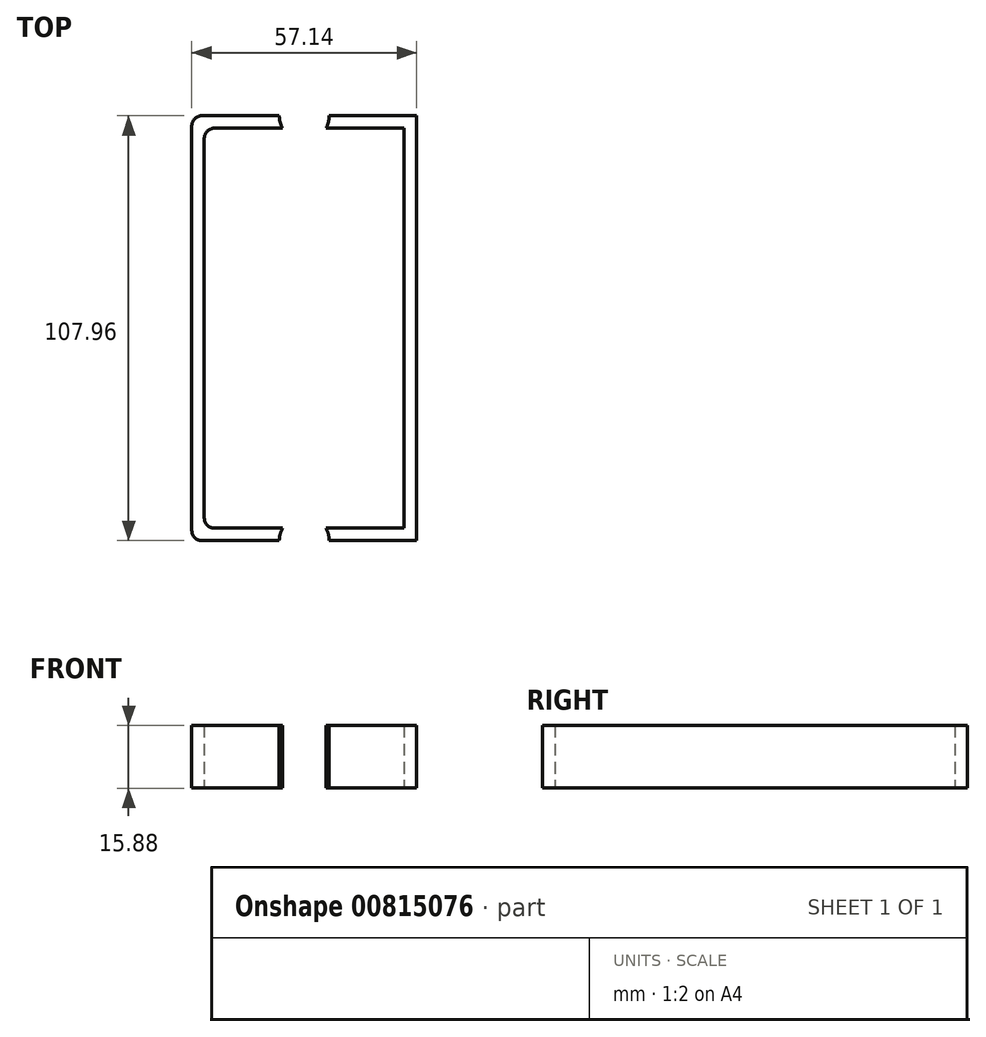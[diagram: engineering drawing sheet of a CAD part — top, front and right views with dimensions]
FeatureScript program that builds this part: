
annotation { "Feature Type Name" : "Feature", "Feature Type Description" : "" }
export const myFeature = defineFeature(function(context is Context, id is Id, definition is map)
    precondition{}
    {
        {
            var Q0;
            Q0=qCreatedBy(makeId("Top.planeOp"),FACE);
            var sketch = newSketch(context, id + "F0", { "sketchPlane" : qUnion([Q0])});
            skLineSegment(sketch, "E0.bottom", {"start": v(-25.4, 50.8) * mm, "end": v(25.4, 50.8) * mm});
            skLineSegment(sketch, "E0.top", {"start": v(-25.4, -50.8) * mm, "end": v(25.4, -50.8) * mm});
            skLineSegment(sketch, "E0.left", {"start": v(-25.4, 50.8) * mm, "end": v(-25.4, -50.8) * mm});
            skLineSegment(sketch, "E0.right", {"start": v(25.4, 50.8) * mm, "end": v(25.4, -50.8) * mm});
            skPoint(sketch, "E0.middle", {"position": v(0, 0) * mm});
            skLineSegment(sketch, "E1.bottom", {"start": v(-28.57, 53.98) * mm, "end": v(28.58, 53.98) * mm});
            skLineSegment(sketch, "E1.top", {"start": v(-28.58, -53.98) * mm, "end": v(28.57, -53.98) * mm});
            skLineSegment(sketch, "E1.left", {"start": v(-28.57, 53.98) * mm, "end": v(-28.58, -53.98) * mm});
            skLineSegment(sketch, "E1.right", {"start": v(28.58, 53.98) * mm, "end": v(28.57, -53.98) * mm});
            skCircle(sketch, "E2", {"center": v(0, 53.98) * mm, "radius": 6.35 * mm});
            skCircle(sketch, "E3", {"center": v(-28.57, 53.98) * mm, "radius": 6.35 * mm});
            skCircle(sketch, "E4", {"center": v(-28.58, -53.98) * mm, "radius": 6.35 * mm});
            skCircle(sketch, "E5", {"center": v(0, -53.98) * mm, "radius": 6.35 * mm});
            skSolve(sketch);
        }
        {
            var Q0;
            {var subQ0=sQuery(id+"F0.wireOp",EDGE,"E1.left");var subQ1=sQuery(id+"F0.wireOp",EDGE,"E1.bottom");var subQ2=makeQuery(id+"F0.imprint","INTERSECT",VERTEX,{"derivedFrom":[subQ1,subQ0]});Q0=makeQuery(id+"F0.imprint","IMPRINT",FACE,{"disambiguationData":[TD([[makeQuery(id+"F0.imprint","IMPRINT",EDGE,{"disambiguationData":[TD([[subQ2,-1.0]])],"derivedFrom":subQ1}),1.0]])]});}
            var Q1;
            {var subQ0=sQuery(id+"F0.wireOp",EDGE,"E2");var subQ1=sQuery(id+"F0.wireOp",EDGE,"E1.bottom");var subQ2=makeQuery(id+"F0.imprint","INTERSECT",VERTEX,{"disambiguationData":[OD(0.0)],"derivedFrom":[subQ1,subQ0]});Q1=makeQuery(id+"F0.imprint","IMPRINT",FACE,{"disambiguationData":[TD([[makeQuery(id+"F0.imprint","IMPRINT",EDGE,{"disambiguationData":[TD([[subQ2,-1.0]])],"derivedFrom":subQ1}),1.0]])]});}
            var Q2;
            {var subQ0=sQuery(id+"F0.wireOp",EDGE,"E1.left");var subQ1=sQuery(id+"F0.wireOp",EDGE,"E1.top");var subQ2=makeQuery(id+"F0.imprint","INTERSECT",VERTEX,{"derivedFrom":[subQ1,subQ0]});Q2=makeQuery(id+"F0.imprint","IMPRINT",FACE,{"disambiguationData":[TD([[makeQuery(id+"F0.imprint","IMPRINT",EDGE,{"disambiguationData":[TD([[subQ2,-1.0]])],"derivedFrom":subQ1}),-1.0]])]});}
            var Q3;
            {var subQ0=sQuery(id+"F0.wireOp",EDGE,"E5");var subQ1=sQuery(id+"F0.wireOp",EDGE,"E1.top");var subQ2=makeQuery(id+"F0.imprint","INTERSECT",VERTEX,{"disambiguationData":[OD(0.0)],"derivedFrom":[subQ1,subQ0]});Q3=makeQuery(id+"F0.imprint","IMPRINT",FACE,{"disambiguationData":[TD([[makeQuery(id+"F0.imprint","IMPRINT",EDGE,{"disambiguationData":[TD([[subQ2,-1.0]])],"derivedFrom":subQ1}),-1.0]])]});}
            var Q4;
            {var subQ0=sQuery(id+"F0.wireOp",EDGE,"E3");var subQ1=sQuery(id+"F0.wireOp",EDGE,"E0.bottom");var subQ2=makeQuery(id+"F0.imprint","INTERSECT",VERTEX,{"derivedFrom":[subQ1,subQ0]});Q4=makeQuery(id+"F0.imprint","IMPRINT",FACE,{"disambiguationData":[TD([[makeQuery(id+"F0.imprint","IMPRINT",EDGE,{"disambiguationData":[TD([[subQ2,-1.0]])],"derivedFrom":subQ1}),1.0]])]});}
            var Q5;
            {var subQ0=sQuery(id+"F0.wireOp",EDGE,"E4");var subQ1=sQuery(id+"F0.wireOp",EDGE,"E0.top");var subQ2=makeQuery(id+"F0.imprint","INTERSECT",VERTEX,{"derivedFrom":[subQ1,subQ0]});Q5=makeQuery(id+"F0.imprint","IMPRINT",FACE,{"disambiguationData":[TD([[makeQuery(id+"F0.imprint","IMPRINT",EDGE,{"disambiguationData":[TD([[subQ2,-1.0]])],"derivedFrom":subQ1}),-1.0]])]});}
            var Q6;
            {var subQ0=sQuery(id+"F0.wireOp",EDGE,"E3");var subQ1=sQuery(id+"F0.wireOp",EDGE,"E0.left");var subQ2=makeQuery(id+"F0.imprint","INTERSECT",VERTEX,{"derivedFrom":[subQ1,subQ0]});Q6=makeQuery(id+"F0.imprint","IMPRINT",FACE,{"disambiguationData":[TD([[makeQuery(id+"F0.imprint","IMPRINT",EDGE,{"disambiguationData":[TD([[subQ2,-1.0]])],"derivedFrom":subQ1}),-1.0]])]});}
            var Q7;
            {var subQ5=sQuery(id+"F0.wireOp",EDGE,"E0.left");var subQ6=sQuery(id+"F0.wireOp",EDGE,"E0.bottom");var subQ7=makeQuery(id+"F0.imprint","INTERSECT",VERTEX,{"derivedFrom":[subQ6,subQ5]});Q7=makeQuery(id+"F0.imprint","IMPRINT",FACE,{"disambiguationData":[TD([[makeQuery(id+"F0.imprint","IMPRINT",EDGE,{"disambiguationData":[TD([[subQ7,-1.0]])],"derivedFrom":subQ6}),1.0]])]});}
            var Q8;
            {var subQ0=sQuery(id+"F0.wireOp",EDGE,"E2");var subQ1=sQuery(id+"F0.wireOp",EDGE,"E0.bottom");var subQ2=makeQuery(id+"F0.imprint","INTERSECT",VERTEX,{"disambiguationData":[OD(0.0)],"derivedFrom":[subQ1,subQ0]});Q8=makeQuery(id+"F0.imprint","IMPRINT",FACE,{"disambiguationData":[TD([[makeQuery(id+"F0.imprint","IMPRINT",EDGE,{"disambiguationData":[TD([[subQ2,-1.0]])],"derivedFrom":subQ1}),1.0]])]});}
            var Q9;
            {var subQ6=sQuery(id+"F0.wireOp",EDGE,"E0.left");var subQ7=sQuery(id+"F0.wireOp",EDGE,"E0.top");var subQ8=makeQuery(id+"F0.imprint","INTERSECT",VERTEX,{"derivedFrom":[subQ7,subQ6]});Q9=makeQuery(id+"F0.imprint","IMPRINT",FACE,{"disambiguationData":[TD([[makeQuery(id+"F0.imprint","IMPRINT",EDGE,{"disambiguationData":[TD([[subQ8,-1.0]])],"derivedFrom":subQ7}),-1.0]])]});}
            var Q10;
            {var subQ0=sQuery(id+"F0.wireOp",EDGE,"E5");var subQ1=sQuery(id+"F0.wireOp",EDGE,"E0.top");var subQ2=makeQuery(id+"F0.imprint","INTERSECT",VERTEX,{"disambiguationData":[OD(0.0)],"derivedFrom":[subQ1,subQ0]});Q10=makeQuery(id+"F0.imprint","IMPRINT",FACE,{"disambiguationData":[TD([[makeQuery(id+"F0.imprint","IMPRINT",EDGE,{"disambiguationData":[TD([[subQ2,-1.0]])],"derivedFrom":subQ1}),-1.0]])]});}
            extrude(context, id + "F1", {"entities" : qUnion([Q0, Q1, Q2, Q3, Q4, Q5, Q6, Q7, Q8, Q9, Q10]), "depth" : 3.17 * mm, "offsetDistance" : 25.4 * mm});
        }
        {
            var Q0;
            {var subQ0=sQuery(id+"F0.wireOp",EDGE,"E3");var subQ1=sQuery(id+"F0.wireOp",EDGE,"E0.bottom");var subQ2=makeQuery(id+"F0.imprint","INTERSECT",VERTEX,{"derivedFrom":[subQ1,subQ0]});Q0=makeQuery(id+"F0.imprint","IMPRINT",FACE,{"disambiguationData":[TD([[makeQuery(id+"F0.imprint","IMPRINT",EDGE,{"disambiguationData":[TD([[subQ2,-1.0]])],"derivedFrom":subQ1}),1.0]])]});}
            var Q1;
            {var subQ0=sQuery(id+"F0.wireOp",EDGE,"E2");var subQ1=sQuery(id+"F0.wireOp",EDGE,"E0.bottom");var subQ2=makeQuery(id+"F0.imprint","INTERSECT",VERTEX,{"disambiguationData":[OD(0.0)],"derivedFrom":[subQ1,subQ0]});Q1=makeQuery(id+"F0.imprint","IMPRINT",FACE,{"disambiguationData":[TD([[makeQuery(id+"F0.imprint","IMPRINT",EDGE,{"disambiguationData":[TD([[subQ2,-1.0]])],"derivedFrom":subQ1}),1.0]])]});}
            var Q2;
            {var subQ5=sQuery(id+"F0.wireOp",EDGE,"E0.left");var subQ6=sQuery(id+"F0.wireOp",EDGE,"E0.bottom");var subQ7=makeQuery(id+"F0.imprint","INTERSECT",VERTEX,{"derivedFrom":[subQ6,subQ5]});Q2=makeQuery(id+"F0.imprint","IMPRINT",FACE,{"disambiguationData":[TD([[makeQuery(id+"F0.imprint","IMPRINT",EDGE,{"disambiguationData":[TD([[subQ7,-1.0]])],"derivedFrom":subQ6}),1.0]])]});}
            var Q3;
            {var subQ0=sQuery(id+"F0.wireOp",EDGE,"E3");var subQ1=sQuery(id+"F0.wireOp",EDGE,"E0.left");var subQ2=makeQuery(id+"F0.imprint","INTERSECT",VERTEX,{"derivedFrom":[subQ1,subQ0]});Q3=makeQuery(id+"F0.imprint","IMPRINT",FACE,{"disambiguationData":[TD([[makeQuery(id+"F0.imprint","IMPRINT",EDGE,{"disambiguationData":[TD([[subQ2,-1.0]])],"derivedFrom":subQ1}),-1.0]])]});}
            var Q4;
            {var subQ6=sQuery(id+"F0.wireOp",EDGE,"E0.left");var subQ7=sQuery(id+"F0.wireOp",EDGE,"E0.top");var subQ8=makeQuery(id+"F0.imprint","INTERSECT",VERTEX,{"derivedFrom":[subQ7,subQ6]});Q4=makeQuery(id+"F0.imprint","IMPRINT",FACE,{"disambiguationData":[TD([[makeQuery(id+"F0.imprint","IMPRINT",EDGE,{"disambiguationData":[TD([[subQ8,-1.0]])],"derivedFrom":subQ7}),-1.0]])]});}
            var Q5;
            {var subQ0=sQuery(id+"F0.wireOp",EDGE,"E4");var subQ1=sQuery(id+"F0.wireOp",EDGE,"E0.top");var subQ2=makeQuery(id+"F0.imprint","INTERSECT",VERTEX,{"derivedFrom":[subQ1,subQ0]});Q5=makeQuery(id+"F0.imprint","IMPRINT",FACE,{"disambiguationData":[TD([[makeQuery(id+"F0.imprint","IMPRINT",EDGE,{"disambiguationData":[TD([[subQ2,-1.0]])],"derivedFrom":subQ1}),-1.0]])]});}
            var Q6;
            {var subQ0=sQuery(id+"F0.wireOp",EDGE,"E5");var subQ1=sQuery(id+"F0.wireOp",EDGE,"E0.top");var subQ2=makeQuery(id+"F0.imprint","INTERSECT",VERTEX,{"disambiguationData":[OD(0.0)],"derivedFrom":[subQ1,subQ0]});Q6=makeQuery(id+"F0.imprint","IMPRINT",FACE,{"disambiguationData":[TD([[makeQuery(id+"F0.imprint","IMPRINT",EDGE,{"disambiguationData":[TD([[subQ2,-1.0]])],"derivedFrom":subQ1}),-1.0]])]});}
            extrude(context, id + "F2", {"entities" : qUnion([Q0, Q1, Q2, Q3, Q4, Q5, Q6]), "operationType" : NewBodyOperationType.ADD, "depth" : 19.05 * mm, "offsetDistance" : 25.4 * mm});
        }
        {
            var Q0;
            {var subQ4=sQuery(id+"F0.wireOp",EDGE,"E0.right");Q0=makeQuery(id+"F0.imprint","IMPRINT",FACE,{"disambiguationData":[TD([[makeQuery(id+"F0.imprint","IMPRINT",EDGE,{"derivedFrom":subQ4}),1.0]])]});}
            var Q1;
            {var subQ0=sQuery(id+"F0.wireOp",EDGE,"E0.right");Q1=makeQuery(id+"F0.imprint","IMPRINT",FACE,{"disambiguationData":[TD([[makeQuery(id+"F0.imprint","IMPRINT",EDGE,{"derivedFrom":subQ0}),-1.0]])]});}
            var Q2;
            {var subQ0=sQuery(id+"F0.wireOp",EDGE,"E2");var subQ1=sQuery(id+"F0.wireOp",EDGE,"E0.bottom");var subQ2=makeQuery(id+"F0.imprint","INTERSECT",VERTEX,{"disambiguationData":[OD(0.0)],"derivedFrom":[subQ1,subQ0]});Q2=makeQuery(id+"F0.imprint","IMPRINT",FACE,{"disambiguationData":[TD([[makeQuery(id+"F0.imprint","IMPRINT",EDGE,{"disambiguationData":[TD([[subQ2,-1.0]])],"derivedFrom":subQ1}),-1.0]])]});}
            var Q3;
            {var subQ0=sQuery(id+"F0.wireOp",EDGE,"E0.left");var subQ1=sQuery(id+"F0.wireOp",EDGE,"E0.bottom");var subQ2=makeQuery(id+"F0.imprint","INTERSECT",VERTEX,{"derivedFrom":[subQ1,subQ0]});Q3=makeQuery(id+"F0.imprint","IMPRINT",FACE,{"disambiguationData":[TD([[makeQuery(id+"F0.imprint","IMPRINT",EDGE,{"disambiguationData":[TD([[subQ2,-1.0]])],"derivedFrom":subQ1}),-1.0]])]});}
            var Q4;
            {var subQ0=sQuery(id+"F0.wireOp",EDGE,"E5");var subQ1=sQuery(id+"F0.wireOp",EDGE,"E0.top");var subQ2=makeQuery(id+"F0.imprint","INTERSECT",VERTEX,{"disambiguationData":[OD(0.0)],"derivedFrom":[subQ1,subQ0]});Q4=makeQuery(id+"F0.imprint","IMPRINT",FACE,{"disambiguationData":[TD([[makeQuery(id+"F0.imprint","IMPRINT",EDGE,{"disambiguationData":[TD([[subQ2,-1.0]])],"derivedFrom":subQ1}),1.0]])]});}
            var Q5;
            {var subQ0=sQuery(id+"F0.wireOp",EDGE,"E0.left");var subQ1=sQuery(id+"F0.wireOp",EDGE,"E0.top");var subQ2=makeQuery(id+"F0.imprint","INTERSECT",VERTEX,{"derivedFrom":[subQ1,subQ0]});Q5=makeQuery(id+"F0.imprint","IMPRINT",FACE,{"disambiguationData":[TD([[makeQuery(id+"F0.imprint","IMPRINT",EDGE,{"disambiguationData":[TD([[subQ2,-1.0]])],"derivedFrom":subQ1}),1.0]])]});}
            extrude(context, id + "F3", {"entities" : qUnion([Q0, Q1, Q2, Q3, Q4, Q5]), "operationType" : NewBodyOperationType.ADD, "depth" : 3.17 * mm, "offsetDistance" : 25.4 * mm});
        }
        {
            var Q0;
            Q0=makeQuery(id+"F3.opExtrude","CAP_EDGE",EDGE,{"disambiguationData":[OSD([sQuery(id+"F0.wireOp",EDGE,"E5")])],"isStart":false});
            var Q1;
            Q1=makeQuery(id+"F3.opExtrude","CAP_EDGE",EDGE,{"disambiguationData":[OSD([sQuery(id+"F0.wireOp",EDGE,"E2")])],"isStart":false});
            chamfer(context, id + "F4", {"entities" : qUnion([Q0, Q1]), "chamferType" : ChamferType.OFFSET_ANGLE, "width" : 16.5 * mm, "oppositeDirection" : false, "angle" : 50 * degree, "tangentPropagation" : true});
        }
        {
            var Q0;
            {var subQ0=sQuery(id+"F0.wireOp",EDGE,"E0.left");var subQ1=sQuery(id+"F0.wireOp",EDGE,"E0.top");Q0=makeQuery(id+"F2.boolean.opBoolean","MERGE",EDGE,{"derivedFrom":[makeQuery(id+"F1.opExtrude","SWEPT_EDGE",EDGE,{"disambiguationData":[OSD([subQ1,subQ0])]}),makeQuery(id+"F2.opExtrude","SWEPT_EDGE",EDGE,{"disambiguationData":[OSD([subQ1,subQ0])]})]});}
            var Q1;
            {var subQ0=sQuery(id+"F0.wireOp",EDGE,"E0.left");var subQ1=sQuery(id+"F0.wireOp",EDGE,"E0.bottom");Q1=makeQuery(id+"F2.boolean.opBoolean","MERGE",EDGE,{"derivedFrom":[makeQuery(id+"F1.opExtrude","SWEPT_EDGE",EDGE,{"disambiguationData":[OSD([subQ1,subQ0])]}),makeQuery(id+"F2.opExtrude","SWEPT_EDGE",EDGE,{"disambiguationData":[OSD([subQ1,subQ0])]})]});}
            var Q2;
            Q2=makeQuery(id+"F2.opExtrude","SWEPT_EDGE",EDGE,{"disambiguationData":[OSD([sQuery(id+"F0.wireOp",EDGE,"E1.top"),sQuery(id+"F0.wireOp",EDGE,"E1.left")])]});
            var Q3;
            Q3=makeQuery(id+"F2.opExtrude","SWEPT_EDGE",EDGE,{"disambiguationData":[OSD([sQuery(id+"F0.wireOp",EDGE,"E1.bottom"),sQuery(id+"F0.wireOp",EDGE,"E1.left")])]});
            fillet(context, id + "F5", {"entities" : qUnion([Q0, Q1, Q2, Q3]), "radius" : 2.54 * mm, "tangentPropagation" : true, "allowEdgeOverflow" : false});
        }
        {
            var Q0;
            Q0=qCreatedBy(makeId("Top.planeOp"),FACE);
            var sketch = newSketch(context, id + "F6", { "sketchPlane" : qUnion([Q0])});
            skLineSegment(sketch, "E6.bottom", {"start": v(-112.62, -109.92) * mm, "end": v(164.85, -109.92) * mm});
            skLineSegment(sketch, "E6.top", {"start": v(-112.62, 145.48) * mm, "end": v(164.85, 145.48) * mm});
            skLineSegment(sketch, "E6.left", {"start": v(-112.62, -109.92) * mm, "end": v(-112.62, 145.48) * mm});
            skLineSegment(sketch, "E6.right", {"start": v(164.85, -109.92) * mm, "end": v(164.85, 145.48) * mm});
            skSolve(sketch);
        }
        {
            var Q0;
            Q0 = qSketchRegion(id + "F6", true);
            extrude(context, id + "F7", {"entities" : qUnion([Q0]), "operationType" : NewBodyOperationType.REMOVE, "depth" : 3.17 * mm, "offsetDistance" : 25.4 * mm});
        }
    });
